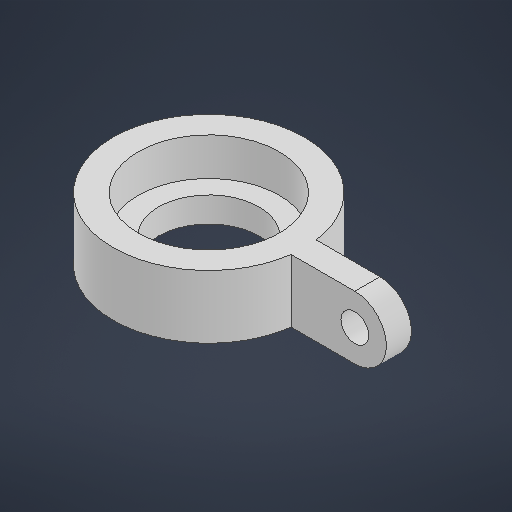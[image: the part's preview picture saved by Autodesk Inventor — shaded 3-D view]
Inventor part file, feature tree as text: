
AUTODESK INVENTOR PART (.ipt)
format: ipt  version: 2025.1 (Build 291241000, 241)  size: 348,160 bytes
history: native  units: mm
features: extrude x3, sketch x2
ambient origin geometry x8: Origin, YZ Plane, XZ Plane, XY Plane, X Axis, Y Axis, Z Axis, Center Point
bodies: Solid1 (feature_tree)
feature tree (5):
  sketch  "Sketch1"  dims[d0=8.0mm d1=11.2mm]
  extrude  "Extrusion1"  Depth=11.2mm
  extrude  "Extrusion2"  Depth=3.0mm TaperAngle=0.0deg
  extrude  "Extrusion3"  Depth=5.0mm
  sketch  "Sketch2"  dims[d3=2.0mm d4=0.0mm d5=3.0mm d6=0.0mm d7=2.2mm d8=5.0mm d11=1.0mm d12=2.0mm d13=0.0mm d14=2.0mm d15=5.0mm]
